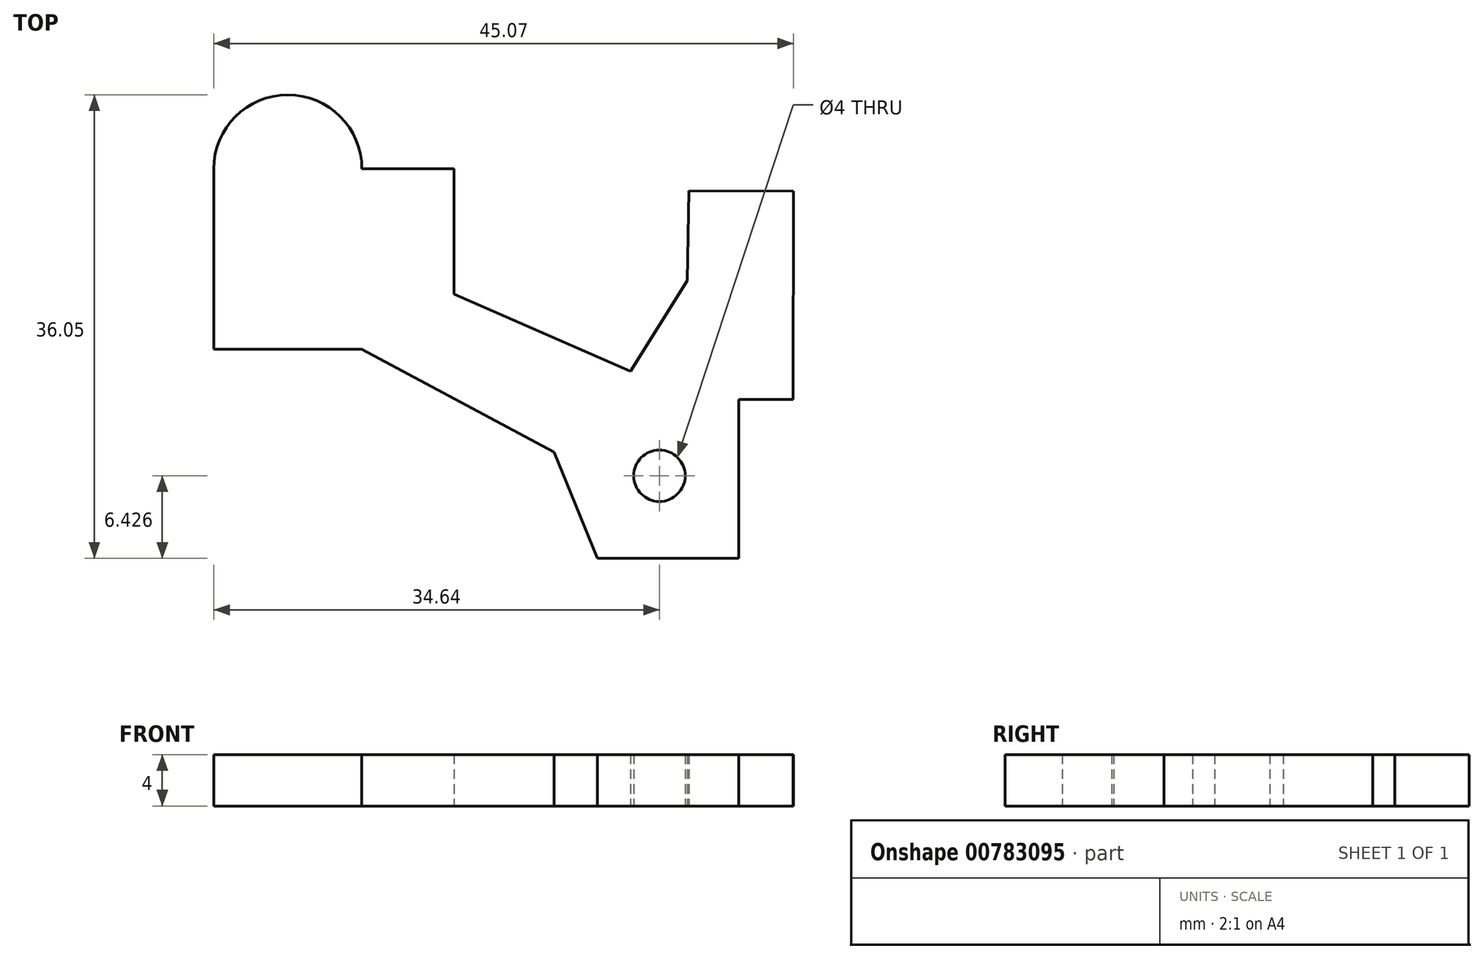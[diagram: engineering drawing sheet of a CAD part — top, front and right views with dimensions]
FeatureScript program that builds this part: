
annotation { "Feature Type Name" : "Feature", "Feature Type Description" : "" }
export const myFeature = defineFeature(function(context is Context, id is Id, definition is map)
    precondition{}
    {
        {
            var Q0;
            Q0=qCreatedBy(makeId("Top.planeOp"),FACE);
            var sketch = newSketch(context, id + "F0", { "sketchPlane" : qUnion([Q0])});
            skLineSegment(sketch, "E0.0", {"start": v(-159.54, 42.4) * mm, "end": v(-148.03, 42.4) * mm});
            skLineSegment(sketch, "E0.1", {"start": v(-133.07, 34.4) * mm, "end": v(-148.03, 42.4) * mm});
            skLineSegment(sketch, "E0.2", {"start": v(-129.7, 26.13) * mm, "end": v(-133.07, 34.4) * mm});
            skLineSegment(sketch, "E0.3", {"start": v(-118.75, 26.13) * mm, "end": v(-129.7, 26.13) * mm});
            skLineSegment(sketch, "E0.4", {"start": v(-118.75, 38.5) * mm, "end": v(-118.75, 26.13) * mm});
            skLineSegment(sketch, "E0.5", {"start": v(-114.52, 38.48) * mm, "end": v(-118.75, 38.5) * mm});
            skLineSegment(sketch, "E1", {"start": v(-114.52, 38.48) * mm, "end": v(-114.47, 54.68) * mm});
            skLineSegment(sketch, "E2", {"start": v(-114.47, 54.68) * mm, "end": v(-122.62, 54.7) * mm});
            skLineSegment(sketch, "E3", {"start": v(-122.73, 47.73) * mm, "end": v(-127.15, 40.68) * mm});
            skLineSegment(sketch, "E4", {"start": v(-159.54, 42.4) * mm, "end": v(-159.54, 56.42) * mm});
            skArc(sketch, "E5", {"start": v(-148.03, 56.42) * mm, "mid": v(-153.78, 62.18) * mm, "end": v(-159.54, 56.42) * mm});
            skLineSegment(sketch, "E6", {"start": v(-122.62, 54.7) * mm, "end": v(-122.73, 47.73) * mm});
            skLineSegment(sketch, "E7", {"start": v(-148.03, 56.42) * mm, "end": v(-140.86, 56.42) * mm});
            skLineSegment(sketch, "E8", {"start": v(-140.86, 56.42) * mm, "end": v(-140.86, 46.68) * mm});
            skLineSegment(sketch, "E9", {"start": v(-140.86, 46.68) * mm, "end": v(-127.15, 40.68) * mm});
            skCircle(sketch, "E10", {"center": v(-124.9, 32.56) * mm, "radius": 2 * mm});
            skSolve(sketch);
        }
        {
            var Q0;
            Q0=makeQuery(id+"F0.imprint","IMPRINT",FACE,{"disambiguationData":[TD([[makeQuery(id+"F0.imprint","IMPRINT",EDGE,{"derivedFrom":sQuery(id+"F0.wireOp",EDGE,"E0.0")}),1.0]])]});
            extrude(context, id + "F1", {"entities" : qUnion([Q0]), "depth" : 4 * mm, "offsetDistance" : 25 * mm});
        }
    });
